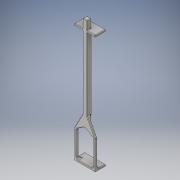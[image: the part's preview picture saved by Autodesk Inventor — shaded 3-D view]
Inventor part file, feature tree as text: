
AUTODESK INVENTOR PART (.ipt)
format: ipt  version: 2016 (Build 200138000, 138)  size: 361,984 bytes
history: native  units: mm
features: extrude x5, sketch x5, fillet x4, projected_geometry x4
ambient origin geometry x8: Origin, YZ Plane, XZ Plane, XY Plane, X Axis, Y Axis, Z Axis, Center Point
bodies: Solid1 (feature_tree)
feature tree (18):
  extrude  "Extrusion1"  Depth=19.8mm
  extrude  "Extrusion2"  Depth=2.0mm
  extrude  "Extrusion3"  Depth=2.0mm
  extrude  "Extrusion4"  Depth=25.0mm TaperAngle=0.0deg
  extrude  "Extrusion5"  Depth=4.0mm
  fillet  "Fillet1"  Radius=15.0mm
  fillet  "Fillet2"  Radius=15.0mm
  fillet  "Fillet3"  Radius=120.0mm
  fillet  "Fillet4"  Radius=15.0mm
  sketch  "Sketch1"  dims[d0=9.8mm d1=19.8mm]
  sketch  "Sketch2"  dims[d2=2.0mm d3=0.0mm d4=2.0mm]
  projected_geometry  "Projected Loop1"
  sketch  "Sketch4"  dims[d5=2.0mm d6=2.0mm]
  projected_geometry  "Projected Loop3"
  sketch  "Sketch6"  dims[d7=2.0mm d8=25.0mm d9=0.0mm]
  projected_geometry  "Projected Loop4"
  sketch  "Sketch7"  dims[d15=5.0mm d16=4.0mm d17=15.0mm d18=15.0mm d19=120.0mm d20=15.0mm d21=0.0mm d22=2.0mm d23=7.0mm d24=78.0mm d25=4.0mm d26=0.0mm d27=110.0mm d28=2.0mm d29=19.8mm d30=4.0mm d31=0.0mm d32=2.0mm d33=0.5mm d34=0.5mm d35=0.5mm]
  projected_geometry  "Projected Loop5"
